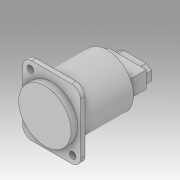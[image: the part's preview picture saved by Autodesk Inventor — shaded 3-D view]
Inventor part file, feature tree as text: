
AUTODESK INVENTOR PART (.ipt)
format: ipt  version: 2019.3 (Build 233278000, 278)  size: 163,328 bytes
history: native  units: mm
features: extrude x5, sketch x5, projected_geometry x4
ambient origin geometry x8: Origin, YZ Plane, XZ Plane, XY Plane, X Axis, Y Axis, Z Axis, Center Point
bodies: Solid1 (feature_tree)
feature tree (14):
  extrude  "Extrusion1"  Depth=31.0mm
  extrude  "Extrusion2"  Depth=2.0mm
  extrude  "Extrusion3"  Depth=2.0mm
  extrude  "Extrusion4"  Depth=4.0mm
  extrude  "Extrusion5"  Depth=3.5mm
  sketch  "Sketch1"  dims[d0=26.0mm d1=31.0mm]
  sketch  "Sketch2"  dims[d2=3.0mm d3=2.0mm]
  projected_geometry  "Projected Loop1"
  sketch  "Sketch3"  dims[d4=2.0mm d5=2.0mm]
  projected_geometry  "Projected Loop2"
  sketch  "Sketch4"  dims[d6=2.0mm d7=4.0mm]
  projected_geometry  "Projected Loop3"
  sketch  "Sketch5"  dims[d8=2.0mm d9=0.0mm d10=23.5mm d11=3.0mm d12=0.0mm d13=23.0mm d14=0.0mm d15=17.0mm d16=7.5mm d17=9.0mm d18=0.0mm d19=5.5mm d20=15.0mm d21=4.0mm d22=10.0mm d23=2.75mm d24=7.5mm d25=3.5mm d26=0.0mm]
  projected_geometry  "Projected Loop4"
